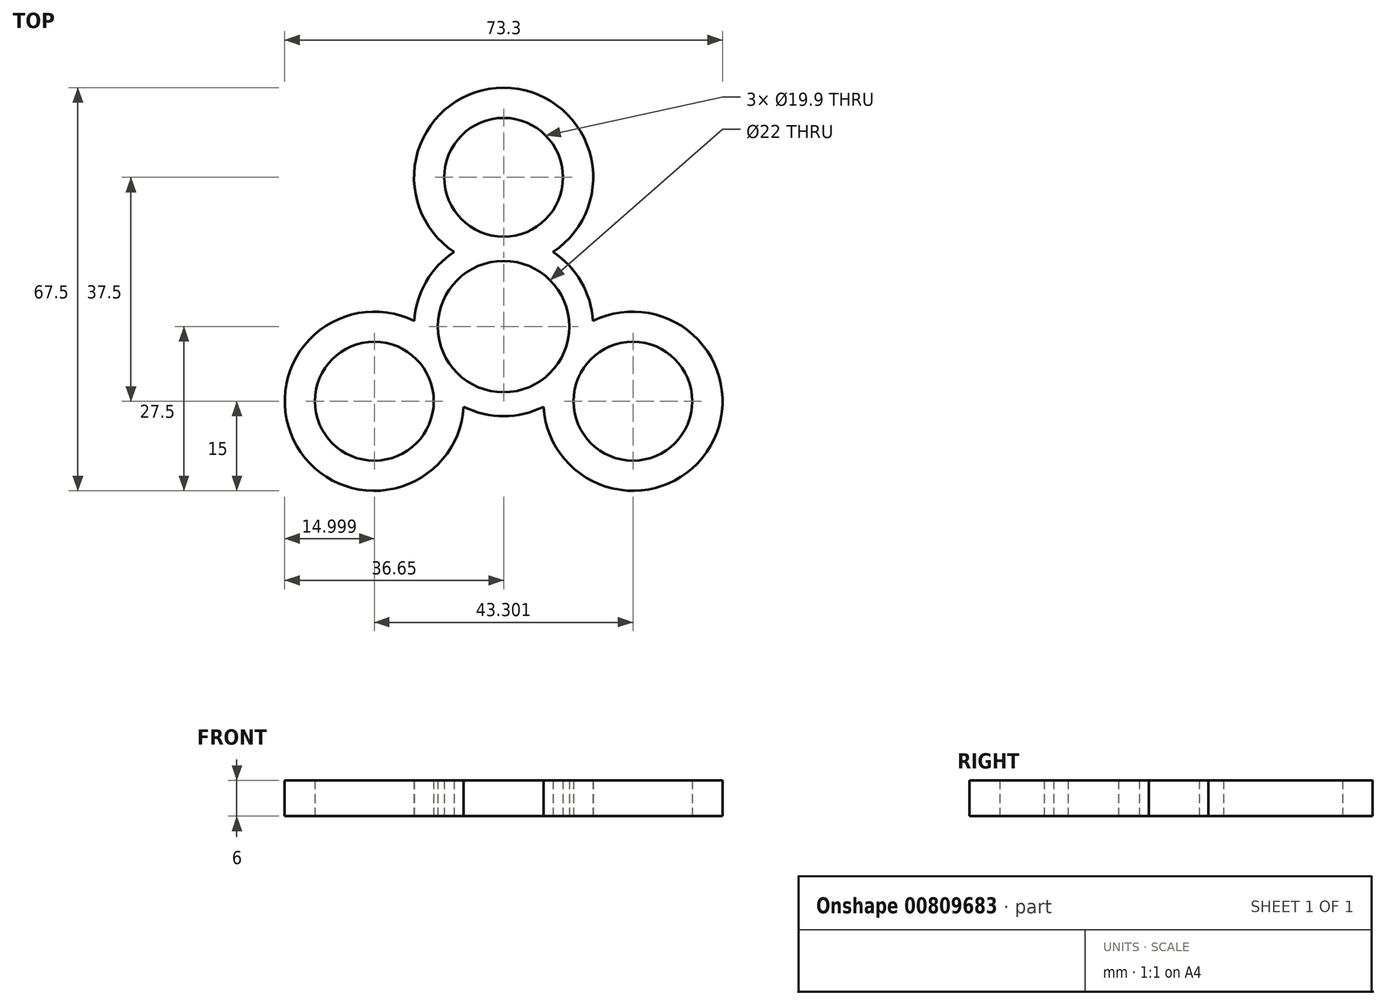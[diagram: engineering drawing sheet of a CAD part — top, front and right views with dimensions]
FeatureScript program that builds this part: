
annotation { "Feature Type Name" : "Feature", "Feature Type Description" : "" }
export const myFeature = defineFeature(function(context is Context, id is Id, definition is map)
    precondition{}
    {
        {
            var Q0;
            Q0=qCreatedBy(makeId("Top.planeOp"),FACE);
            var sketch = newSketch(context, id + "F0", { "sketchPlane" : qUnion([Q0])});
            skArc(sketch, "E0", {"start": v(9.53, 5.5) * mm, "mid": v(0, 11) * mm, "end": v(-9.53, 5.5) * mm});
            skLineSegment(sketch, "E1", {"start": v(0, 0) * mm, "end": v(0, 25) * mm});
            skCircle(sketch, "E2", {"center": v(0, 25) * mm, "radius": 9.95 * mm});
            skArc(sketch, "E3", {"start": v(-8.3, 12.5) * mm, "mid": v(-10.93, 10.27) * mm, "end": v(-13, 7.5) * mm});
            skArc(sketch, "E4.trimOffspring", {"start": v(8.3, 12.5) * mm, "mid": v(0, 40) * mm, "end": v(-8.3, 12.5) * mm});
            skArc(sketch, "E5.trimOffspring", {"start": v(13, 7.5) * mm, "mid": v(10.93, 10.27) * mm, "end": v(8.3, 12.5) * mm});
            skArc(sketch, "E6.1.0", {"start": v(-9.53, 5.5) * mm, "mid": v(-9.53, -5.5) * mm, "end": v(0, -11) * mm});
            skArc(sketch, "E6.1.1", {"start": v(-6.68, -13.43) * mm, "mid": v(-3.43, -14.6) * mm, "end": v(0, -15) * mm});
            skArc(sketch, "E6.1.2", {"start": v(-14.97, 0.93) * mm, "mid": v(-34.64, -20) * mm, "end": v(-6.68, -13.43) * mm});
            skCircle(sketch, "E6.1.3", {"center": v(-21.65, -12.5) * mm, "radius": 9.95 * mm});
            skArc(sketch, "E6.1.4", {"start": v(-13, 7.5) * mm, "mid": v(-14.36, 4.33) * mm, "end": v(-14.97, 0.93) * mm});
            skArc(sketch, "E6.2.0", {"start": v(0, -11) * mm, "mid": v(9.53, -5.5) * mm, "end": v(9.53, 5.5) * mm});
            skArc(sketch, "E6.2.1", {"start": v(14.97, 0.93) * mm, "mid": v(14.36, 4.33) * mm, "end": v(13, 7.5) * mm});
            skArc(sketch, "E6.2.2", {"start": v(6.68, -13.43) * mm, "mid": v(34.64, -20) * mm, "end": v(14.97, 0.93) * mm});
            skCircle(sketch, "E6.2.3", {"center": v(21.65, -12.5) * mm, "radius": 9.95 * mm});
            skArc(sketch, "E6.2.4", {"start": v(0, -15) * mm, "mid": v(3.43, -14.6) * mm, "end": v(6.68, -13.43) * mm});
            skSolve(sketch);
        }
        {
            var Q0;
            Q0 = qSketchRegion(id + "F0", true);
            extrude(context, id + "F1", {"entities" : qUnion([Q0]), "depth" : 6 * mm, "offsetDistance" : 25 * mm});
        }
    });
